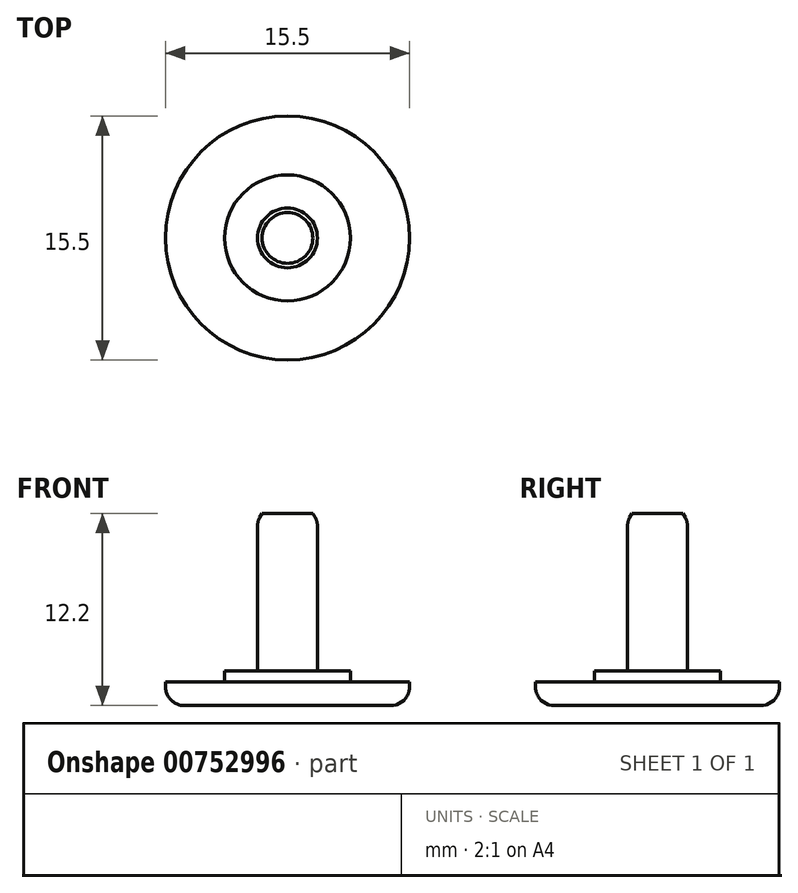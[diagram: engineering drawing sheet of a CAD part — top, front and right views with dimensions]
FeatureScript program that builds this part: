
annotation { "Feature Type Name" : "Feature", "Feature Type Description" : "" }
export const myFeature = defineFeature(function(context is Context, id is Id, definition is map)
    precondition{}
    {
        {
            var Q0;
            Q0=qCreatedBy(makeId("Front.planeOp"),FACE);
            var sketch = newSketch(context, id + "F0", { "sketchPlane" : qUnion([Q0])});
            skLineSegment(sketch, "E0", {"start": v(0, 0) * mm, "end": v(-7.75, 0) * mm});
            skLineSegment(sketch, "E1", {"start": v(-7.75, 0) * mm, "end": v(-7.75, 1.5) * mm});
            skLineSegment(sketch, "E2", {"start": v(-7.75, 1.5) * mm, "end": v(-4, 1.5) * mm});
            skLineSegment(sketch, "E3", {"start": v(-1.9, 2.2) * mm, "end": v(-1.9, 12.2) * mm});
            skLineSegment(sketch, "E4", {"start": v(-1.9, 12.2) * mm, "end": v(0, 12.2) * mm});
            skLineSegment(sketch, "E5", {"start": v(0, 12.2) * mm, "end": v(0, 0) * mm});
            skLineSegment(sketch, "E6", {"start": v(0, 0) * mm, "end": v(0, 10.15) * mm, "construction": true});
            skLineSegment(sketch, "E7", {"start": v(-4, 1.5) * mm, "end": v(-4, 2.2) * mm});
            skLineSegment(sketch, "E8", {"start": v(-4, 2.2) * mm, "end": v(-1.9, 2.2) * mm});
            skSolve(sketch);
        }
        {
            var Q0;
            Q0 = qSketchRegion(id + "F0", true);
            var Q1;
            Q1=sQuery(id+"F0.wireOp",EDGE,"E6");
            revolve(context, id + "F1", {"surfaceOperationType" : NewSurfaceOperationType.NEW, "entities" : qUnion([Q0]), "axis" : qUnion([Q1]), "revolveType" : RevolveType.FULL});
        }
        {
            var Q0;
            Q0=makeQuery(id+"F1.opRevolve","SWEPT_EDGE",EDGE,{"disambiguationData":[OSD([sQuery(id+"F0.wireOp",EDGE,"E0"),sQuery(id+"F0.wireOp",EDGE,"E1")])]});
            fillet(context, id + "F2", {"entities" : qUnion([Q0]), "radius" : 1.2 * mm, "tangentPropagation" : true, "allowEdgeOverflow" : false});
        }
        {
            var Q0;
            Q0=makeQuery(id+"F1.opRevolve","SWEPT_EDGE",EDGE,{"disambiguationData":[OSD([sQuery(id+"F0.wireOp",EDGE,"E3"),sQuery(id+"F0.wireOp",EDGE,"E4")])]});
            chamfer(context, id + "F3", {"entities" : qUnion([Q0]), "chamferType" : ChamferType.OFFSET_ANGLE, "width" : .5 * mm, "oppositeDirection" : false, "angle" : 30 * degree, "tangentPropagation" : true});
        }
        {
            var Q0;
            {var subQ0=sQuery(id+"F0.wireOp",EDGE,"E3");Q0=makeQuery(id+"F3.opChamfer","BLEND_EDGE",EDGE,{"blendedFrom":[makeQuery(id+"F1.opRevolve","SWEPT_EDGE",EDGE,{"disambiguationData":[OSD([subQ0,sQuery(id+"F0.wireOp",EDGE,"E4")])]}),makeQuery(id+"F1.opRevolve","SWEPT_FACE",FACE,{"disambiguationData":[OSD([subQ0])]})],"blendedInto":[makeQuery(id+"F1.opRevolve","SWEPT_FACE",FACE,{"disambiguationData":[OSD([subQ0])]})]});}
            fillet(context, id + "F4", {"entities" : qUnion([Q0]), "radius" : 1 * mm, "tangentPropagation" : true, "allowEdgeOverflow" : false});
        }
    });
